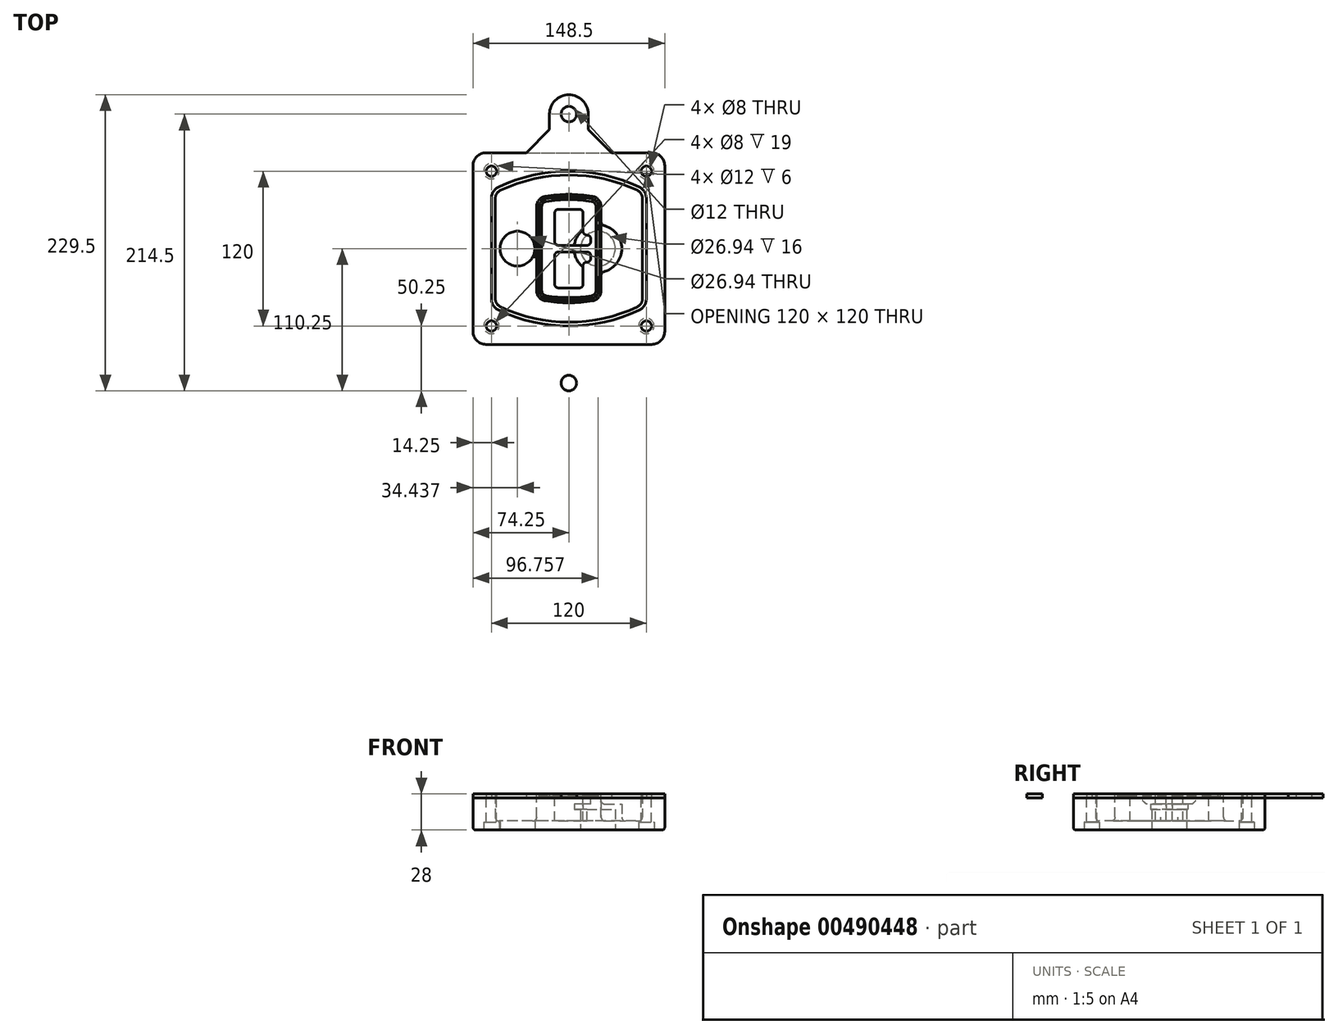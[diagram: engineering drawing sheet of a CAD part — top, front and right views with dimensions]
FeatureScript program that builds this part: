
annotation { "Feature Type Name" : "Feature", "Feature Type Description" : "" }
export const myFeature = defineFeature(function(context is Context, id is Id, definition is map)
    precondition{}
    {
        {
            var Q0;
            Q0=qCreatedBy(makeId("Top.planeOp"),FACE);
            var sketch = newSketch(context, id + "F0", { "sketchPlane" : qUnion([Q0])});
            skPoint(sketch, "E0.rect.middle", {"position": v(0, 0) * mm});
            skLineSegment(sketch, "E1.bottom", {"start": v(-64.25, -74.25) * mm, "end": v(64.25, -74.25) * mm});
            skLineSegment(sketch, "E1.top", {"start": v(-64.25, 74.25) * mm, "end": v(64.25, 74.25) * mm});
            skLineSegment(sketch, "E1.left", {"start": v(-74.25, -64.25) * mm, "end": v(-74.25, 64.25) * mm});
            skLineSegment(sketch, "E1.right", {"start": v(74.25, -64.25) * mm, "end": v(74.25, 64.25) * mm});
            skLineSegment(sketch, "E2", {"start": v(-74.25, 74.25) * mm, "end": v(74.25, -74.25) * mm, "construction": true});
            skLineSegment(sketch, "E3", {"start": v(74.25, 74.25) * mm, "end": v(-74.25, -74.25) * mm, "construction": true});
            skCircle(sketch, "E4", {"center": v(-60, 60) * mm, "radius": 4 * mm});
            skCircle(sketch, "E5", {"center": v(60, 60) * mm, "radius": 4 * mm});
            skCircle(sketch, "E6", {"center": v(60, -60) * mm, "radius": 4 * mm});
            skCircle(sketch, "E7", {"center": v(-60, -60) * mm, "radius": 4 * mm});
            skLineSegment(sketch, "E8", {"start": v(-60, 60) * mm, "end": v(60, 60) * mm, "construction": true});
            skLineSegment(sketch, "E9", {"start": v(60, 60) * mm, "end": v(60, -60) * mm, "construction": true});
            skLineSegment(sketch, "E10", {"start": v(60, -60) * mm, "end": v(-60, -60) * mm, "construction": true});
            skLineSegment(sketch, "E11", {"start": v(-60, -60) * mm, "end": v(-60, 60) * mm, "construction": true});
            skLineSegment(sketch, "E12", {"start": v(-60, 38.83) * mm, "end": v(-60, -38.83) * mm});
            skLineSegment(sketch, "E13", {"start": v(60, 38.83) * mm, "end": v(60, -38.83) * mm});
            skArc(sketch, "E14", {"start": v(54.26, 47.88) * mm, "mid": v(0, 60) * mm, "end": v(-54.26, 47.88) * mm});
            skArc(sketch, "E15", {"start": v(-54.26, -47.88) * mm, "mid": v(0, -60) * mm, "end": v(54.26, -47.88) * mm});
            skLineSegment(sketch, "E16", {"start": v(-60, 0) * mm, "end": v(60, 0) * mm, "construction": true});
            skPoint(sketch, "E17.visualSharp", {"position": v(-60, -45) * mm});
            skArc(sketch, "E17.filletArc", {"start": v(-60, -38.83) * mm, "mid": v(-58.44, -44.2) * mm, "end": v(-54.26, -47.88) * mm});
            skPoint(sketch, "E18.visualSharp", {"position": v(-60, 45) * mm});
            skArc(sketch, "E18.filletArc", {"start": v(-54.26, 47.88) * mm, "mid": v(-58.44, 44.2) * mm, "end": v(-60, 38.83) * mm});
            skPoint(sketch, "E19.visualSharp", {"position": v(60, 45) * mm});
            skArc(sketch, "E19.filletArc", {"start": v(60, 38.83) * mm, "mid": v(58.44, 44.2) * mm, "end": v(54.26, 47.88) * mm});
            skPoint(sketch, "E20.visualSharp", {"position": v(60, -45) * mm});
            skArc(sketch, "E20.filletArc", {"start": v(54.26, -47.88) * mm, "mid": v(58.44, -44.2) * mm, "end": v(60, -38.83) * mm});
            skPoint(sketch, "E21.visualSharp", {"position": v(-74.25, 74.25) * mm});
            skArc(sketch, "E21.filletArc", {"start": v(-64.25, 74.25) * mm, "mid": v(-71.32, 71.32) * mm, "end": v(-74.25, 64.25) * mm});
            skPoint(sketch, "E22.visualSharp", {"position": v(74.25, 74.25) * mm});
            skArc(sketch, "E22.filletArc", {"start": v(74.25, 64.25) * mm, "mid": v(71.32, 71.32) * mm, "end": v(64.25, 74.25) * mm});
            skPoint(sketch, "E23.visualSharp", {"position": v(74.25, -74.25) * mm});
            skArc(sketch, "E23.filletArc", {"start": v(64.25, -74.25) * mm, "mid": v(71.32, -71.32) * mm, "end": v(74.25, -64.25) * mm});
            skPoint(sketch, "E24.visualSharp", {"position": v(-74.25, -74.25) * mm});
            skArc(sketch, "E24.filletArc", {"start": v(-74.25, -64.25) * mm, "mid": v(-71.32, -71.32) * mm, "end": v(-64.25, -74.25) * mm});
            skArc(sketch, "E25.0", {"start": v(57, 38.83) * mm, "mid": v(55.9, 42.58) * mm, "end": v(52.98, 45.17) * mm});
            skLineSegment(sketch, "E25.1", {"start": v(57, 38.83) * mm, "end": v(57, -38.83) * mm});
            skArc(sketch, "E25.2", {"start": v(52.98, -45.17) * mm, "mid": v(55.9, -42.58) * mm, "end": v(57, -38.83) * mm});
            skArc(sketch, "E25.3", {"start": v(-52.98, -45.17) * mm, "mid": v(0, -57) * mm, "end": v(52.98, -45.17) * mm});
            skArc(sketch, "E25.4", {"start": v(-57, -38.83) * mm, "mid": v(-55.9, -42.58) * mm, "end": v(-52.98, -45.17) * mm});
            skArc(sketch, "E25.5", {"start": v(52.98, 45.17) * mm, "mid": v(0, 57) * mm, "end": v(-52.98, 45.17) * mm});
            skLineSegment(sketch, "E25.6", {"start": v(-57, 38.83) * mm, "end": v(-57, -38.83) * mm});
            skArc(sketch, "E25.7", {"start": v(-52.98, 45.17) * mm, "mid": v(-55.9, 42.58) * mm, "end": v(-57, 38.83) * mm});
            skArc(sketch, "E26.0", {"start": v(-55.96, 51.5) * mm, "mid": v(-61.82, 46.33) * mm, "end": v(-64, 38.83) * mm});
            skArc(sketch, "E26.1", {"start": v(55.96, 51.5) * mm, "mid": v(0, 64) * mm, "end": v(-55.96, 51.5) * mm});
            skArc(sketch, "E26.2", {"start": v(64, 38.83) * mm, "mid": v(61.82, 46.33) * mm, "end": v(55.96, 51.5) * mm});
            skLineSegment(sketch, "E26.3", {"start": v(64, 38.83) * mm, "end": v(64, -38.83) * mm});
            skArc(sketch, "E26.4", {"start": v(55.96, -51.5) * mm, "mid": v(61.82, -46.33) * mm, "end": v(64, -38.83) * mm});
            skLineSegment(sketch, "E26.5", {"start": v(-64, 38.83) * mm, "end": v(-64, -38.83) * mm});
            skArc(sketch, "E26.6", {"start": v(-55.96, -51.5) * mm, "mid": v(0, -64) * mm, "end": v(55.96, -51.5) * mm});
            skArc(sketch, "E26.7", {"start": v(-64, -38.83) * mm, "mid": v(-61.82, -46.33) * mm, "end": v(-55.96, -51.5) * mm});
            skSolve(sketch);
        }
        {
            var Q0;
            Q0=makeQuery(id+"F0.imprint","IMPRINT",FACE,{"disambiguationData":[TD([[makeQuery(id+"F0.imprint","IMPRINT",EDGE,{"derivedFrom":sQuery(id+"F0.wireOp",EDGE,"E1.bottom")}),1.0]])]});
            var Q1;
            Q1=makeQuery(id+"F0.imprint","IMPRINT",FACE,{"disambiguationData":[TD([[makeQuery(id+"F0.imprint","IMPRINT",EDGE,{"derivedFrom":sQuery(id+"F0.wireOp",EDGE,"E12")}),1.0]])]});
            var Q2;
            Q2=makeQuery(id+"F0.imprint","IMPRINT",FACE,{"disambiguationData":[TD([[makeQuery(id+"F0.imprint","IMPRINT",EDGE,{"derivedFrom":sQuery(id+"F0.wireOp",EDGE,"E25.0")}),1.0]])]});
            var Q3;
            Q3=makeQuery(id+"F0.imprint","IMPRINT",FACE,{"disambiguationData":[TD([[makeQuery(id+"F0.imprint","IMPRINT",EDGE,{"derivedFrom":sQuery(id+"F0.wireOp",EDGE,"E12")}),-1.0]])]});
            extrude(context, id + "F1", {"entities" : qUnion([Q0, Q1, Q2, Q3]), "oppositeDirection" : true, "depth" : 25 * mm});
        }
        {
            var Q0;
            Q0=makeQuery(id+"F0.imprint","IMPRINT",FACE,{"disambiguationData":[TD([[makeQuery(id+"F0.imprint","IMPRINT",EDGE,{"derivedFrom":sQuery(id+"F0.wireOp",EDGE,"E12")}),1.0]])]});
            extrude(context, id + "F2", {"entities" : qUnion([Q0]), "operationType" : NewBodyOperationType.ADD, "depth" : 3 * mm});
        }
        {
            var Q0;
            Q0=makeQuery(id+"F0.imprint","IMPRINT",FACE,{"disambiguationData":[TD([[makeQuery(id+"F0.imprint","IMPRINT",EDGE,{"derivedFrom":sQuery(id+"F0.wireOp",EDGE,"E25.0")}),1.0]])]});
            extrude(context, id + "F3", {"entities" : qUnion([Q0]), "operationType" : NewBodyOperationType.REMOVE, "oppositeDirection" : true, "depth" : 18 * mm});
        }
        {
            var Q0;
            Q0=makeQuery(id+"F2.opExtrude","CAP_FACE",FACE,{"disambiguationData":[OSD([sQuery(id+"F0.wireOp",EDGE,"E12"),sQuery(id+"F0.wireOp",EDGE,"E13"),sQuery(id+"F0.wireOp",EDGE,"E14"),sQuery(id+"F0.wireOp",EDGE,"E15"),sQuery(id+"F0.wireOp",EDGE,"E17.filletArc"),sQuery(id+"F0.wireOp",EDGE,"E18.filletArc"),sQuery(id+"F0.wireOp",EDGE,"E19.filletArc"),sQuery(id+"F0.wireOp",EDGE,"E20.filletArc"),sQuery(id+"F0.wireOp",EDGE,"E25.0"),sQuery(id+"F0.wireOp",EDGE,"E25.1"),sQuery(id+"F0.wireOp",EDGE,"E25.2"),sQuery(id+"F0.wireOp",EDGE,"E25.3"),sQuery(id+"F0.wireOp",EDGE,"E25.4"),sQuery(id+"F0.wireOp",EDGE,"E25.5"),sQuery(id+"F0.wireOp",EDGE,"E25.6"),sQuery(id+"F0.wireOp",EDGE,"E25.7")])],"isStart":false});
            var sketch = newSketch(context, id + "F4", { "sketchPlane" : qUnion([Q0])});
            skArc(sketch, "E27.0", {"start": v(-18.34, -40.45) * mm, "mid": v(0, -42) * mm, "end": v(18.34, -40.45) * mm});
            skArc(sketch, "E28.0", {"start": v(18.34, 40.45) * mm, "mid": v(0, 42) * mm, "end": v(-18.34, 40.45) * mm});
            skLineSegment(sketch, "E29", {"start": v(-25, 32.57) * mm, "end": v(-25, -32.57) * mm});
            skLineSegment(sketch, "E30", {"start": v(25, 32.57) * mm, "end": v(25, -32.57) * mm});
            skLineSegment(sketch, "E31", {"start": v(-25, 39.1) * mm, "end": v(25, 39.1) * mm, "construction": true});
            skLineSegment(sketch, "E32", {"start": v(-25, -39.1) * mm, "end": v(25, -39.1) * mm, "construction": true});
            skPoint(sketch, "E33.visualSharp", {"position": v(-25, 39.1) * mm});
            skArc(sketch, "E33.filletArc", {"start": v(-18.34, 40.45) * mm, "mid": v(-23.11, 37.73) * mm, "end": v(-25, 32.57) * mm});
            skPoint(sketch, "E34.visualSharp", {"position": v(25, 39.1) * mm});
            skArc(sketch, "E34.filletArc", {"start": v(25, 32.57) * mm, "mid": v(23.11, 37.73) * mm, "end": v(18.34, 40.45) * mm});
            skPoint(sketch, "E35.visualSharp", {"position": v(25, -39.1) * mm});
            skArc(sketch, "E35.filletArc", {"start": v(18.34, -40.45) * mm, "mid": v(23.11, -37.73) * mm, "end": v(25, -32.57) * mm});
            skPoint(sketch, "E36.visualSharp", {"position": v(-25, -39.1) * mm});
            skArc(sketch, "E36.filletArc", {"start": v(-25, -32.57) * mm, "mid": v(-23.11, -37.73) * mm, "end": v(-18.34, -40.45) * mm});
            skArc(sketch, "E37.0", {"start": v(52.98, 45.17) * mm, "mid": v(0, 57) * mm, "end": v(-52.98, 45.17) * mm});
            skArc(sketch, "E37.1", {"start": v(-52.98, 45.17) * mm, "mid": v(-55.9, 42.58) * mm, "end": v(-57, 38.83) * mm});
            skLineSegment(sketch, "E37.2", {"start": v(-57, 38.83) * mm, "end": v(-57, -38.83) * mm});
            skArc(sketch, "E37.3", {"start": v(-57, -38.83) * mm, "mid": v(-55.9, -42.58) * mm, "end": v(-52.98, -45.17) * mm});
            skArc(sketch, "E37.4", {"start": v(-52.98, -45.17) * mm, "mid": v(0, -57) * mm, "end": v(52.98, -45.17) * mm});
            skArc(sketch, "E37.5", {"start": v(52.98, -45.17) * mm, "mid": v(55.9, -42.58) * mm, "end": v(57, -38.83) * mm});
            skLineSegment(sketch, "E37.6", {"start": v(57, 38.83) * mm, "end": v(57, -38.83) * mm});
            skArc(sketch, "E37.7", {"start": v(57, 38.83) * mm, "mid": v(55.9, 42.58) * mm, "end": v(52.98, 45.17) * mm});
            skLineSegment(sketch, "E38.0", {"start": v(23, 32.57) * mm, "end": v(23, -32.57) * mm});
            skArc(sketch, "E38.1", {"start": v(18, -38.48) * mm, "mid": v(21.58, -36.44) * mm, "end": v(23, -32.57) * mm});
            skArc(sketch, "E38.2", {"start": v(-18, -38.48) * mm, "mid": v(0, -40) * mm, "end": v(18, -38.48) * mm});
            skArc(sketch, "E38.3", {"start": v(-23, -32.57) * mm, "mid": v(-21.58, -36.44) * mm, "end": v(-18, -38.48) * mm});
            skLineSegment(sketch, "E38.4", {"start": v(-23, 32.57) * mm, "end": v(-23, -32.57) * mm});
            skArc(sketch, "E38.5", {"start": v(23, 32.57) * mm, "mid": v(21.58, 36.44) * mm, "end": v(18, 38.48) * mm});
            skArc(sketch, "E38.6", {"start": v(-18, 38.48) * mm, "mid": v(-21.58, 36.44) * mm, "end": v(-23, 32.57) * mm});
            skArc(sketch, "E38.7", {"start": v(18, 38.48) * mm, "mid": v(0, 40) * mm, "end": v(-18, 38.48) * mm});
            skArc(sketch, "E39.0", {"start": v(21, 32.57) * mm, "mid": v(20.06, 35.15) * mm, "end": v(17.67, 36.5) * mm});
            skLineSegment(sketch, "E39.1", {"start": v(21, 32.57) * mm, "end": v(21, -32.57) * mm});
            skArc(sketch, "E39.2", {"start": v(17.67, -36.5) * mm, "mid": v(20.06, -35.15) * mm, "end": v(21, -32.57) * mm});
            skArc(sketch, "E39.3", {"start": v(-17.67, -36.5) * mm, "mid": v(0, -38) * mm, "end": v(17.67, -36.5) * mm});
            skArc(sketch, "E39.4", {"start": v(-21, -32.57) * mm, "mid": v(-20.06, -35.15) * mm, "end": v(-17.67, -36.5) * mm});
            skArc(sketch, "E39.5", {"start": v(17.67, 36.5) * mm, "mid": v(0, 38) * mm, "end": v(-17.67, 36.5) * mm});
            skLineSegment(sketch, "E39.6", {"start": v(-21, 32.57) * mm, "end": v(-21, -32.57) * mm});
            skArc(sketch, "E39.7", {"start": v(-17.67, 36.5) * mm, "mid": v(-20.06, 35.15) * mm, "end": v(-21, 32.57) * mm});
            skLineSegment(sketch, "E40", {"start": v(-25, 0) * mm, "end": v(25, 0) * mm, "construction": true});
            skLineSegment(sketch, "E41", {"start": v(-11, 5.5) * mm, "end": v(-11, 27.5) * mm});
            skLineSegment(sketch, "E42", {"start": v(-8, 30.5) * mm, "end": v(8, 30.5) * mm});
            skLineSegment(sketch, "E43", {"start": v(11, 27.5) * mm, "end": v(11, 13.5) * mm});
            skLineSegment(sketch, "E44", {"start": v(14, 10.5) * mm, "end": v(14, 10.5) * mm});
            skLineSegment(sketch, "E45", {"start": v(17, 7.5) * mm, "end": v(17, 5.5) * mm});
            skLineSegment(sketch, "E46", {"start": v(14, 2.5) * mm, "end": v(-8, 2.5) * mm});
            skPoint(sketch, "E47.visualSharp", {"position": v(-11, 30.5) * mm});
            skArc(sketch, "E47.filletArc", {"start": v(-8, 30.5) * mm, "mid": v(-10.12, 29.62) * mm, "end": v(-11, 27.5) * mm});
            skPoint(sketch, "E48.visualSharp", {"position": v(11, 30.5) * mm});
            skArc(sketch, "E48.filletArc", {"start": v(11, 27.5) * mm, "mid": v(10.12, 29.62) * mm, "end": v(8, 30.5) * mm});
            skPoint(sketch, "E49.visualSharp", {"position": v(11, 10.5) * mm});
            skArc(sketch, "E49.filletArc", {"start": v(11, 13.5) * mm, "mid": v(11.88, 11.38) * mm, "end": v(14, 10.5) * mm});
            skPoint(sketch, "E50.visualSharp", {"position": v(17, 10.5) * mm});
            skArc(sketch, "E50.filletArc", {"start": v(17, 7.5) * mm, "mid": v(16.12, 9.62) * mm, "end": v(14, 10.5) * mm});
            skPoint(sketch, "E51.visualSharp", {"position": v(17, 2.5) * mm});
            skArc(sketch, "E51.filletArc", {"start": v(14, 2.5) * mm, "mid": v(16.12, 3.38) * mm, "end": v(17, 5.5) * mm});
            skPoint(sketch, "E52.visualSharp", {"position": v(-11, 2.5) * mm});
            skArc(sketch, "E52.filletArc", {"start": v(-11, 5.5) * mm, "mid": v(-10.12, 3.38) * mm, "end": v(-8, 2.5) * mm});
            skLineSegment(sketch, "E53.0.MirrorCS", {"start": v(14, -2.5) * mm, "end": v(-8, -2.5) * mm});
            skArc(sketch, "E54.0.MirrorCS", {"start": v(-11, -5.5) * mm, "mid": v(-10.12, -3.38) * mm, "end": v(-8, -2.5) * mm});
            skLineSegment(sketch, "E55.0.MirrorCS", {"start": v(-11, -5.5) * mm, "end": v(-11, -27.5) * mm});
            skArc(sketch, "E56.0.MirrorCS", {"start": v(-8, -30.5) * mm, "mid": v(-10.12, -29.62) * mm, "end": v(-11, -27.5) * mm});
            skLineSegment(sketch, "E57.0.MirrorCS", {"start": v(-8, -30.5) * mm, "end": v(8, -30.5) * mm});
            skArc(sketch, "E58.0.MirrorCS", {"start": v(11, -27.5) * mm, "mid": v(10.12, -29.62) * mm, "end": v(8, -30.5) * mm});
            skLineSegment(sketch, "E59.0.MirrorCS", {"start": v(11, -27.5) * mm, "end": v(11, -13.5) * mm});
            skArc(sketch, "E60.0.MirrorCS", {"start": v(11, -13.5) * mm, "mid": v(11.88, -11.38) * mm, "end": v(14, -10.5) * mm});
            skArc(sketch, "E61.0.MirrorCS", {"start": v(17, -7.5) * mm, "mid": v(16.12, -9.62) * mm, "end": v(14, -10.5) * mm});
            skLineSegment(sketch, "E62.0.MirrorCS", {"start": v(17, -7.5) * mm, "end": v(17, -5.5) * mm});
            skArc(sketch, "E63.0.MirrorCS", {"start": v(14, -2.5) * mm, "mid": v(16.12, -3.38) * mm, "end": v(17, -5.5) * mm});
            skSolve(sketch);
        }
        {
            var Q0;
            Q0=makeQuery(id+"F4.imprint","IMPRINT",FACE,{"disambiguationData":[TD([[makeQuery(id+"F4.imprint","IMPRINT",EDGE,{"derivedFrom":sQuery(id+"F4.wireOp",EDGE,"E27.0")}),1.0]])]});
            var Q1;
            Q1=makeQuery(id+"F4.imprint","IMPRINT",FACE,{"disambiguationData":[TD([[makeQuery(id+"F4.imprint","IMPRINT",EDGE,{"derivedFrom":sQuery(id+"F4.wireOp",EDGE,"E38.0")}),-1.0]])]});
            var Q2;
            Q2=makeQuery(id+"F4.imprint","IMPRINT",FACE,{"disambiguationData":[TD([[makeQuery(id+"F4.imprint","IMPRINT",EDGE,{"derivedFrom":sQuery(id+"F4.wireOp",EDGE,"E39.0")}),1.0]])]});
            extrude(context, id + "F5", {"entities" : qUnion([Q0, Q1, Q2]), "operationType" : NewBodyOperationType.ADD, "endBound" : BoundingType.UP_TO_NEXT, "oppositeDirection" : true, "depth" : 25 * mm});
        }
        {
            var Q0;
            Q0=makeQuery(id+"F4.imprint","IMPRINT",FACE,{"disambiguationData":[TD([[makeQuery(id+"F4.imprint","IMPRINT",EDGE,{"derivedFrom":sQuery(id+"F4.wireOp",EDGE,"E38.0")}),-1.0]])]});
            extrude(context, id + "F6", {"entities" : qUnion([Q0]), "operationType" : NewBodyOperationType.REMOVE, "oppositeDirection" : true, "depth" : 2 * mm});
        }
        {
            var Q0;
            Q0=makeQuery(id+"F1.opExtrude","CAP_FACE",FACE,{"disambiguationData":[OSD([sQuery(id+"F0.wireOp",EDGE,"E1.bottom"),sQuery(id+"F0.wireOp",EDGE,"E1.top"),sQuery(id+"F0.wireOp",EDGE,"E1.left"),sQuery(id+"F0.wireOp",EDGE,"E1.right"),sQuery(id+"F0.wireOp",EDGE,"E4"),sQuery(id+"F0.wireOp",EDGE,"E5"),sQuery(id+"F0.wireOp",EDGE,"E6"),sQuery(id+"F0.wireOp",EDGE,"E7"),sQuery(id+"F0.wireOp",EDGE,"E21.filletArc"),sQuery(id+"F0.wireOp",EDGE,"E22.filletArc"),sQuery(id+"F0.wireOp",EDGE,"E23.filletArc"),sQuery(id+"F0.wireOp",EDGE,"E24.filletArc")])],"isStart":false});
            var sketch = newSketch(context, id + "F7", { "sketchPlane" : qUnion([Q0])});
            skCircle(sketch, "E64", {"center": v(22.5, 0) * mm, "radius": 13.47 * mm});
            skCircle(sketch, "E65", {"center": v(-39.81, 0) * mm, "radius": 13.47 * mm});
            skLineSegment(sketch, "E66", {"start": v(74.25, 0) * mm, "end": v(-74.25, 0) * mm});
            skCircle(sketch, "E67", {"center": v(22.5, 0) * mm, "radius": 18.47 * mm});
            skCircle(sketch, "E68", {"center": v(60, -60) * mm, "radius": 6 * mm});
            skCircle(sketch, "E69", {"center": v(-60, -60) * mm, "radius": 6 * mm});
            skCircle(sketch, "E70", {"center": v(-60, 60) * mm, "radius": 6 * mm});
            skCircle(sketch, "E71", {"center": v(60, 60) * mm, "radius": 6 * mm});
            skSolve(sketch);
        }
        {
            var Q0;
            {var subQ1=sQuery(id+"F7.wireOp",EDGE,"E66");var subQ4=sQuery(id+"F7.wireOp",EDGE,"E64");var subQ6=makeQuery(id+"F7.imprint","INTERSECT",VERTEX,{"disambiguationData":[OD(0.0)],"derivedFrom":[subQ4,subQ1]});Q0=makeQuery(id+"F7.imprint","IMPRINT",FACE,{"disambiguationData":[TD([[makeQuery(id+"F7.imprint","IMPRINT",EDGE,{"disambiguationData":[TD([[subQ6,-1.0]])],"derivedFrom":subQ4}),-1.0]])]});}
            var Q1;
            {var subQ0=sQuery(id+"F7.wireOp",EDGE,"E66");var subQ1=sQuery(id+"F7.wireOp",EDGE,"E64");var subQ3=makeQuery(id+"F7.imprint","INTERSECT",VERTEX,{"disambiguationData":[OD(0.0)],"derivedFrom":[subQ1,subQ0]});Q1=makeQuery(id+"F7.imprint","IMPRINT",FACE,{"disambiguationData":[TD([[makeQuery(id+"F7.imprint","IMPRINT",EDGE,{"disambiguationData":[TD([[subQ3,-1.0]])],"derivedFrom":subQ1}),1.0]])]});}
            var Q2;
            {var subQ0=sQuery(id+"F7.wireOp",EDGE,"E66");var subQ1=sQuery(id+"F7.wireOp",EDGE,"E64");var subQ3=makeQuery(id+"F7.imprint","INTERSECT",VERTEX,{"disambiguationData":[OD(0.0)],"derivedFrom":[subQ1,subQ0]});Q2=makeQuery(id+"F7.imprint","IMPRINT",FACE,{"disambiguationData":[TD([[makeQuery(id+"F7.imprint","IMPRINT",EDGE,{"disambiguationData":[TD([[subQ3,1.0]])],"derivedFrom":subQ1}),1.0]])]});}
            var Q3;
            {var subQ1=sQuery(id+"F7.wireOp",EDGE,"E66");var subQ4=sQuery(id+"F7.wireOp",EDGE,"E64");var subQ6=makeQuery(id+"F7.imprint","INTERSECT",VERTEX,{"disambiguationData":[OD(0.0)],"derivedFrom":[subQ4,subQ1]});Q3=makeQuery(id+"F7.imprint","IMPRINT",FACE,{"disambiguationData":[TD([[makeQuery(id+"F7.imprint","IMPRINT",EDGE,{"disambiguationData":[TD([[subQ6,1.0]])],"derivedFrom":subQ4}),-1.0]])]});}
            extrude(context, id + "F8", {"entities" : qUnion([Q0, Q1, Q2, Q3]), "operationType" : NewBodyOperationType.ADD, "oppositeDirection" : true, "depth" : 20 * mm});
        }
        {
            var Q0;
            {var subQ0=sQuery(id+"F7.wireOp",EDGE,"E66");var subQ1=sQuery(id+"F7.wireOp",EDGE,"E64");var subQ3=makeQuery(id+"F7.imprint","INTERSECT",VERTEX,{"disambiguationData":[OD(0.0)],"derivedFrom":[subQ1,subQ0]});Q0=makeQuery(id+"F7.imprint","IMPRINT",FACE,{"disambiguationData":[TD([[makeQuery(id+"F7.imprint","IMPRINT",EDGE,{"disambiguationData":[TD([[subQ3,-1.0]])],"derivedFrom":subQ1}),1.0]])]});}
            var Q1;
            {var subQ0=sQuery(id+"F7.wireOp",EDGE,"E66");var subQ1=sQuery(id+"F7.wireOp",EDGE,"E64");var subQ3=makeQuery(id+"F7.imprint","INTERSECT",VERTEX,{"disambiguationData":[OD(0.0)],"derivedFrom":[subQ1,subQ0]});Q1=makeQuery(id+"F7.imprint","IMPRINT",FACE,{"disambiguationData":[TD([[makeQuery(id+"F7.imprint","IMPRINT",EDGE,{"disambiguationData":[TD([[subQ3,1.0]])],"derivedFrom":subQ1}),1.0]])]});}
            extrude(context, id + "F9", {"entities" : qUnion([Q0, Q1]), "operationType" : NewBodyOperationType.REMOVE, "oppositeDirection" : true, "depth" : 16 * mm});
        }
        {
            var Q0;
            {var subQ0=sQuery(id+"F7.wireOp",EDGE,"E66");var subQ1=sQuery(id+"F7.wireOp",EDGE,"E65");var subQ3=makeQuery(id+"F7.imprint","INTERSECT",VERTEX,{"disambiguationData":[OD(0.0)],"derivedFrom":[subQ1,subQ0]});Q0=makeQuery(id+"F7.imprint","IMPRINT",FACE,{"disambiguationData":[TD([[makeQuery(id+"F7.imprint","IMPRINT",EDGE,{"disambiguationData":[TD([[subQ3,-1.0]])],"derivedFrom":subQ1}),1.0]])]});}
            var Q1;
            {var subQ0=sQuery(id+"F7.wireOp",EDGE,"E66");var subQ1=sQuery(id+"F7.wireOp",EDGE,"E65");var subQ3=makeQuery(id+"F7.imprint","INTERSECT",VERTEX,{"disambiguationData":[OD(0.0)],"derivedFrom":[subQ1,subQ0]});Q1=makeQuery(id+"F7.imprint","IMPRINT",FACE,{"disambiguationData":[TD([[makeQuery(id+"F7.imprint","IMPRINT",EDGE,{"disambiguationData":[TD([[subQ3,1.0]])],"derivedFrom":subQ1}),1.0]])]});}
            extrude(context, id + "F10", {"entities" : qUnion([Q0, Q1]), "operationType" : NewBodyOperationType.REMOVE, "oppositeDirection" : true, "depth" : 25 * mm});
        }
        {
            var Q0;
            Q0=makeQuery(id+"F7.imprint","IMPRINT",FACE,{"disambiguationData":[TD([[makeQuery(id+"F7.imprint","IMPRINT",EDGE,{"derivedFrom":sQuery(id+"F7.wireOp",EDGE,"E68")}),1.0]])]});
            var Q1;
            Q1=makeQuery(id+"F7.imprint","IMPRINT",FACE,{"disambiguationData":[TD([[makeQuery(id+"F7.imprint","IMPRINT",EDGE,{"derivedFrom":makeQuery(id+"F1.opExtrude","CAP_EDGE",EDGE,{"disambiguationData":[OSD([sQuery(id+"F0.wireOp",EDGE,"E5")])],"isStart":false})}),-1.0]])]});
            var Q2;
            Q2=makeQuery(id+"F7.imprint","IMPRINT",FACE,{"disambiguationData":[TD([[makeQuery(id+"F7.imprint","IMPRINT",EDGE,{"derivedFrom":sQuery(id+"F7.wireOp",EDGE,"E69")}),1.0]])]});
            var Q3;
            Q3=makeQuery(id+"F7.imprint","IMPRINT",FACE,{"disambiguationData":[TD([[makeQuery(id+"F7.imprint","IMPRINT",EDGE,{"derivedFrom":makeQuery(id+"F1.opExtrude","CAP_EDGE",EDGE,{"disambiguationData":[OSD([sQuery(id+"F0.wireOp",EDGE,"E4")])],"isStart":false})}),-1.0]])]});
            var Q4;
            Q4=makeQuery(id+"F7.imprint","IMPRINT",FACE,{"disambiguationData":[TD([[makeQuery(id+"F7.imprint","IMPRINT",EDGE,{"derivedFrom":sQuery(id+"F7.wireOp",EDGE,"E70")}),1.0]])]});
            var Q5;
            Q5=makeQuery(id+"F7.imprint","IMPRINT",FACE,{"disambiguationData":[TD([[makeQuery(id+"F7.imprint","IMPRINT",EDGE,{"derivedFrom":makeQuery(id+"F1.opExtrude","CAP_EDGE",EDGE,{"disambiguationData":[OSD([sQuery(id+"F0.wireOp",EDGE,"E7")])],"isStart":false})}),-1.0]])]});
            var Q6;
            Q6=makeQuery(id+"F7.imprint","IMPRINT",FACE,{"disambiguationData":[TD([[makeQuery(id+"F7.imprint","IMPRINT",EDGE,{"derivedFrom":sQuery(id+"F7.wireOp",EDGE,"E71")}),1.0]])]});
            var Q7;
            Q7=makeQuery(id+"F7.imprint","IMPRINT",FACE,{"disambiguationData":[TD([[makeQuery(id+"F7.imprint","IMPRINT",EDGE,{"derivedFrom":makeQuery(id+"F1.opExtrude","CAP_EDGE",EDGE,{"disambiguationData":[OSD([sQuery(id+"F0.wireOp",EDGE,"E6")])],"isStart":false})}),-1.0]])]});
            extrude(context, id + "F11", {"entities" : qUnion([Q0, Q1, Q2, Q3, Q4, Q5, Q6, Q7]), "operationType" : NewBodyOperationType.REMOVE, "oppositeDirection" : true, "depth" : 6 * mm});
        }
        {
            var Q0;
            Q0=makeQuery(id+"F9.boolean.opBoolean","COPY",FACE,{"derivedFrom":makeQuery(id+"F9.opExtrude","CAP_FACE",FACE,{"disambiguationData":[OSD([sQuery(id+"F7.wireOp",EDGE,"E64")])],"isStart":false})});
            var sketch = newSketch(context, id + "F12", { "sketchPlane" : qUnion([Q0])});
            skArc(sketch, "E72.0", {"start": v(11, 14.45) * mm, "mid": v(6.45, 9.13) * mm, "end": v(4.2, 2.5) * mm});
            skArc(sketch, "E72.1", {"start": v(4.2, -2.5) * mm, "mid": v(6.45, -9.13) * mm, "end": v(11, -14.45) * mm});
            skLineSegment(sketch, "E73", {"start": v(4.2, -2.5) * mm, "end": v(14, -2.5) * mm});
            skLineSegment(sketch, "E74.0", {"start": v(14, 2.5) * mm, "end": v(4.2, 2.5) * mm});
            skArc(sketch, "E74.1", {"start": v(14, 2.5) * mm, "mid": v(16.12, 3.38) * mm, "end": v(17, 5.5) * mm});
            skLineSegment(sketch, "E74.2", {"start": v(17, 7.5) * mm, "end": v(17, 5.5) * mm});
            skArc(sketch, "E74.3", {"start": v(17, 7.5) * mm, "mid": v(16.12, 9.62) * mm, "end": v(14, 10.5) * mm});
            skArc(sketch, "E74.4", {"start": v(11, 13.5) * mm, "mid": v(11.88, 11.38) * mm, "end": v(14, 10.5) * mm});
            skLineSegment(sketch, "E74.5", {"start": v(11, 14.45) * mm, "end": v(11, 13.5) * mm});
            skLineSegment(sketch, "E74.7", {"start": v(14, -2.5) * mm, "end": v(4.2, -2.5) * mm});
            skArc(sketch, "E74.8", {"start": v(14, -2.5) * mm, "mid": v(16.12, -3.38) * mm, "end": v(17, -5.5) * mm});
            skLineSegment(sketch, "E74.9", {"start": v(17, -7.5) * mm, "end": v(17, -5.5) * mm});
            skArc(sketch, "E74.10", {"start": v(17, -7.5) * mm, "mid": v(16.12, -9.62) * mm, "end": v(14, -10.5) * mm});
            skArc(sketch, "E74.11", {"start": v(11, -13.5) * mm, "mid": v(11.88, -11.38) * mm, "end": v(14, -10.5) * mm});
            skLineSegment(sketch, "E74.12", {"start": v(11, -14.45) * mm, "end": v(11, -13.5) * mm});
            skPoint(sketch, "E75.orphan", {"position": v(11, -27.5) * mm});
            skPoint(sketch, "E76.orphan", {"position": v(-8, -2.5) * mm});
            skPoint(sketch, "E77.orphan", {"position": v(-8, 2.5) * mm});
            skPoint(sketch, "E78.orphan", {"position": v(11, 27.5) * mm});
            skSolve(sketch);
        }
        {
            var Q0;
            {var subQ7=sQuery(id+"F12.wireOp",EDGE,"E72.0");var subQ14=sQuery(id+"F12.wireOp",EDGE,"E72.1");var subQ16=sQuery(id+"F12.wireOp",EDGE,"E74.1");var subQ18=sQuery(id+"F12.wireOp",EDGE,"E74.8");Q0=qUnion([makeQuery(id+"F12.imprint","IMPRINT",FACE,{"disambiguationData":[TD([[makeQuery(id+"F12.imprint","IMPRINT",EDGE,{"derivedFrom":subQ7}),1.0]])]}),makeQuery(id+"F12.imprint","IMPRINT",FACE,{"disambiguationData":[TD([[makeQuery(id+"F12.imprint","IMPRINT",EDGE,{"derivedFrom":subQ14}),1.0]])]}),makeQuery(id+"F12.imprint","IMPRINT",FACE,{"disambiguationData":[TD([[makeQuery(id+"F12.imprint","IMPRINT",EDGE,{"derivedFrom":subQ16}),1.0]])]}),makeQuery(id+"F12.imprint","IMPRINT",FACE,{"disambiguationData":[TD([[makeQuery(id+"F12.imprint","IMPRINT",EDGE,{"derivedFrom":subQ18}),-1.0]])]})]);}
            var Q1;
            Q1=makeQuery(id+"F5.boolean.opBoolean","SPLIT",FACE,{"disambiguationData":[TD([makeQuery(id+"F5.opExtrude","SWEPT_FACE",FACE,{"disambiguationData":[OSD([sQuery(id+"F4.wireOp",EDGE,"E41")])]})])],"derivedFrom":makeQuery(id+"F3.boolean.opBoolean","COPY",FACE,{"derivedFrom":makeQuery(id+"F3.opExtrude","CAP_FACE",FACE,{"disambiguationData":[OSD([sQuery(id+"F0.wireOp",EDGE,"E25.0"),sQuery(id+"F0.wireOp",EDGE,"E25.1"),sQuery(id+"F0.wireOp",EDGE,"E25.2"),sQuery(id+"F0.wireOp",EDGE,"E25.3"),sQuery(id+"F0.wireOp",EDGE,"E25.4"),sQuery(id+"F0.wireOp",EDGE,"E25.5"),sQuery(id+"F0.wireOp",EDGE,"E25.6"),sQuery(id+"F0.wireOp",EDGE,"E25.7")])],"isStart":false})})});
            extrude(context, id + "F13", {"entities" : qUnion([Q0]), "operationType" : NewBodyOperationType.REMOVE, "endBound" : BoundingType.UP_TO_SURFACE, "endBoundEntityFace" : qUnion([Q1]), "depth" : 25 * mm});
        }
        {
            var Q0;
            Q0=makeQuery(id+"F3.boolean.opBoolean","COPY",EDGE,{"derivedFrom":makeQuery(id+"F3.opExtrude","CAP_EDGE",EDGE,{"disambiguationData":[OSD([sQuery(id+"F0.wireOp",EDGE,"E25.6")])],"isStart":false})});
            var Q1;
            Q1=makeQuery(id+"F8.boolean.opBoolean","INTERSECT",EDGE,{"derivedFrom":[makeQuery(id+"F5.opExtrude","SWEPT_FACE",FACE,{"disambiguationData":[OSD([sQuery(id+"F4.wireOp",EDGE,"E30")])]}),makeQuery(id+"F8.opExtrude","CAP_FACE",FACE,{"disambiguationData":[OSD([sQuery(id+"F7.wireOp",EDGE,"E67")])],"isStart":false})]});
            var Q2;
            Q2=makeQuery(id+"F8.boolean.opBoolean","INTERSECT",EDGE,{"disambiguationData":[OD(1.0)],"derivedFrom":[makeQuery(id+"F5.opExtrude","SWEPT_FACE",FACE,{"disambiguationData":[OSD([sQuery(id+"F4.wireOp",EDGE,"E30")])]}),makeQuery(id+"F8.opExtrude","SWEPT_FACE",FACE,{"disambiguationData":[OSD([sQuery(id+"F7.wireOp",EDGE,"E67")])]})]});
            var Q3;
            {var subQ0=sQuery(id+"F4.wireOp",EDGE,"E30");Q3=makeQuery(id+"F8.boolean.opBoolean","SPLIT",EDGE,{"disambiguationData":[TD([makeQuery(id+"F5.opExtrude","SWEPT_FACE",FACE,{"disambiguationData":[OSD([sQuery(id+"F4.wireOp",EDGE,"E35.filletArc")])]})])],"derivedFrom":makeQuery(id+"F5.opExtrude","CAP_EDGE",EDGE,{"disambiguationData":[OSD([subQ0])],"isStart":false})});}
            var Q4;
            {var subQ0=sQuery(id+"F0.wireOp",EDGE,"E25.7");var subQ1=sQuery(id+"F0.wireOp",EDGE,"E25.1");var subQ2=sQuery(id+"F0.wireOp",EDGE,"E25.6");var subQ3=sQuery(id+"F0.wireOp",EDGE,"E25.5");var subQ4=sQuery(id+"F0.wireOp",EDGE,"E25.4");var subQ5=sQuery(id+"F0.wireOp",EDGE,"E25.0");var subQ6=sQuery(id+"F0.wireOp",EDGE,"E25.2");var subQ7=sQuery(id+"F0.wireOp",EDGE,"E25.3");Q4=makeQuery(id+"F8.boolean.opBoolean","INTERSECT",EDGE,{"derivedFrom":[makeQuery(id+"F5.boolean.opBoolean","SPLIT",FACE,{"disambiguationData":[TD([makeQuery(id+"F2.opExtrude","SWEPT_FACE",FACE,{"disambiguationData":[OSD([subQ5])]})])],"derivedFrom":makeQuery(id+"F3.boolean.opBoolean","COPY",FACE,{"derivedFrom":makeQuery(id+"F3.opExtrude","CAP_FACE",FACE,{"disambiguationData":[OSD([subQ5,subQ1,subQ6,subQ7,subQ4,subQ3,subQ2,subQ0])],"isStart":false})})}),makeQuery(id+"F8.opExtrude","SWEPT_FACE",FACE,{"disambiguationData":[OSD([sQuery(id+"F7.wireOp",EDGE,"E67")])]})]});}
            var Q5;
            Q5=makeQuery(id+"F8.boolean.opBoolean","INTERSECT",EDGE,{"disambiguationData":[OD(0.0)],"derivedFrom":[makeQuery(id+"F5.opExtrude","SWEPT_FACE",FACE,{"disambiguationData":[OSD([sQuery(id+"F4.wireOp",EDGE,"E30")])]}),makeQuery(id+"F8.opExtrude","SWEPT_FACE",FACE,{"disambiguationData":[OSD([sQuery(id+"F7.wireOp",EDGE,"E67")])]})]});
            fillet(context, id + "F14", {"entities" : qUnion([Q0, Q1, Q2, Q3, Q4, Q5]), "radius" : 3 * mm, "tangentPropagation" : true, "allowEdgeOverflow" : false});
        }
        {
            var Q0;
            Q0=makeQuery(id+"F1.opExtrude","CAP_EDGE",EDGE,{"disambiguationData":[OSD([sQuery(id+"F0.wireOp",EDGE,"E1.bottom")])],"isStart":false});
            fillet(context, id + "F15", {"entities" : qUnion([Q0]), "radius" : 2 * mm, "tangentPropagation" : true, "allowEdgeOverflow" : false});
        }
        {
            var Q0;
            {var subQ0=sQuery(id+"F0.wireOp",EDGE,"E21.filletArc");var subQ1=sQuery(id+"F0.wireOp",EDGE,"E7");var subQ2=sQuery(id+"F0.wireOp",EDGE,"E6");var subQ3=sQuery(id+"F0.wireOp",EDGE,"E5");var subQ4=sQuery(id+"F0.wireOp",EDGE,"E4");var subQ5=sQuery(id+"F0.wireOp",EDGE,"E22.filletArc");var subQ6=sQuery(id+"F0.wireOp",EDGE,"E1.bottom");var subQ7=sQuery(id+"F0.wireOp",EDGE,"E1.right");var subQ8=sQuery(id+"F0.wireOp",EDGE,"E1.top");var subQ9=sQuery(id+"F0.wireOp",EDGE,"E1.left");var subQ10=sQuery(id+"F0.wireOp",EDGE,"E23.filletArc");var subQ11=sQuery(id+"F0.wireOp",EDGE,"E24.filletArc");Q0=makeQuery(id+"F2.boolean.opBoolean","SPLIT",FACE,{"disambiguationData":[TD([makeQuery(id+"F1.opExtrude","SWEPT_FACE",FACE,{"disambiguationData":[OSD([subQ6])]})])],"derivedFrom":makeQuery(id+"F1.opExtrude","CAP_FACE",FACE,{"disambiguationData":[OSD([subQ6,subQ8,subQ9,subQ7,subQ4,subQ3,subQ2,subQ1,subQ0,subQ5,subQ10,subQ11])],"isStart":true})});}
            var sketch = newSketch(context, id + "F16", { "sketchPlane" : qUnion([Q0])});
            skLineSegment(sketch, "E79", {"start": v(0, 74.25) * mm, "end": v(0, 104.25) * mm, "construction": true});
            skArc(sketch, "E80", {"start": v(15, 104.25) * mm, "mid": v(0, 119.25) * mm, "end": v(-15, 104.25) * mm});
            skLineSegment(sketch, "E81", {"start": v(15, 104.25) * mm, "end": v(15, 92.25) * mm});
            skLineSegment(sketch, "E82", {"start": v(-15, 104.25) * mm, "end": v(-15, 92.25) * mm});
            skLineSegment(sketch, "E83", {"start": v(-15, 92.25) * mm, "end": v(-33, 74.25) * mm});
            skLineSegment(sketch, "E84", {"start": v(15, 92.25) * mm, "end": v(33, 74.25) * mm});
            skCircle(sketch, "E85", {"center": v(0, 104.25) * mm, "radius": 6 * mm});
            skLineSegment(sketch, "E86", {"start": v(-74.25, 0) * mm, "end": v(74.25, 0) * mm, "construction": true});
            skCircle(sketch, "E87.MirrorC", {"center": v(0, -104.25) * mm, "radius": 6 * mm});
            skLineSegment(sketch, "E88.MirrorCS", {"start": v(15, -92.25) * mm, "end": v(33, -74.25) * mm});
            skLineSegment(sketch, "E89.MirrorCS", {"start": v(-15, -92.25) * mm, "end": v(-33, -74.25) * mm});
            skLineSegment(sketch, "E90.MirrorCS", {"start": v(-15, -104.25) * mm, "end": v(-15, -92.25) * mm});
            skLineSegment(sketch, "E91.MirrorCS", {"start": v(0, -74.25) * mm, "end": v(0, -104.25) * mm, "construction": true});
            skArc(sketch, "E92.MirrorCS", {"start": v(15, -104.25) * mm, "mid": v(0, -119.25) * mm, "end": v(-15, -104.25) * mm});
            skLineSegment(sketch, "E93.MirrorCS", {"start": v(15, -104.25) * mm, "end": v(15, -92.25) * mm});
            skSolve(sketch);
        }
        {
            var Q0;
            Q0=makeQuery(id+"F16.imprint","IMPRINT",FACE,{"disambiguationData":[TD([[makeQuery(id+"F16.imprint","IMPRINT",EDGE,{"derivedFrom":sQuery(id+"F16.wireOp",EDGE,"E80")}),1.0]])]});
            var Q1;
            Q1=makeQuery(id+"F16.imprint","IMPRINT",FACE,{"disambiguationData":[TD([[makeQuery(id+"F16.imprint","IMPRINT",EDGE,{"derivedFrom":makeQuery(id+"F1.opExtrude","CAP_EDGE",EDGE,{"disambiguationData":[OSD([sQuery(id+"F0.wireOp",EDGE,"E1.left")])],"isStart":true})}),-1.0]])]});
            var Q2;
            Q2=makeQuery(id+"F16.imprint","IMPRINT",FACE,{"disambiguationData":[TD([[makeQuery(id+"F16.imprint","IMPRINT",EDGE,{"derivedFrom":sQuery(id+"F16.wireOp",EDGE,"E87.MirrorC")}),1.0]])]});
            var Q3;
            Q3=makeQuery(id+"F2.opExtrude","CAP_FACE",FACE,{"disambiguationData":[OSD([sQuery(id+"F0.wireOp",EDGE,"E12"),sQuery(id+"F0.wireOp",EDGE,"E13"),sQuery(id+"F0.wireOp",EDGE,"E14"),sQuery(id+"F0.wireOp",EDGE,"E15"),sQuery(id+"F0.wireOp",EDGE,"E17.filletArc"),sQuery(id+"F0.wireOp",EDGE,"E18.filletArc"),sQuery(id+"F0.wireOp",EDGE,"E19.filletArc"),sQuery(id+"F0.wireOp",EDGE,"E20.filletArc"),sQuery(id+"F0.wireOp",EDGE,"E25.0"),sQuery(id+"F0.wireOp",EDGE,"E25.1"),sQuery(id+"F0.wireOp",EDGE,"E25.2"),sQuery(id+"F0.wireOp",EDGE,"E25.3"),sQuery(id+"F0.wireOp",EDGE,"E25.4"),sQuery(id+"F0.wireOp",EDGE,"E25.5"),sQuery(id+"F0.wireOp",EDGE,"E25.6"),sQuery(id+"F0.wireOp",EDGE,"E25.7")])],"isStart":false});
            extrude(context, id + "F17", {"entities" : qUnion([Q0, Q1, Q2]), "endBound" : BoundingType.UP_TO_SURFACE, "endBoundEntityFace" : qUnion([Q3]), "depth" : 25 * mm});
        }
    });
